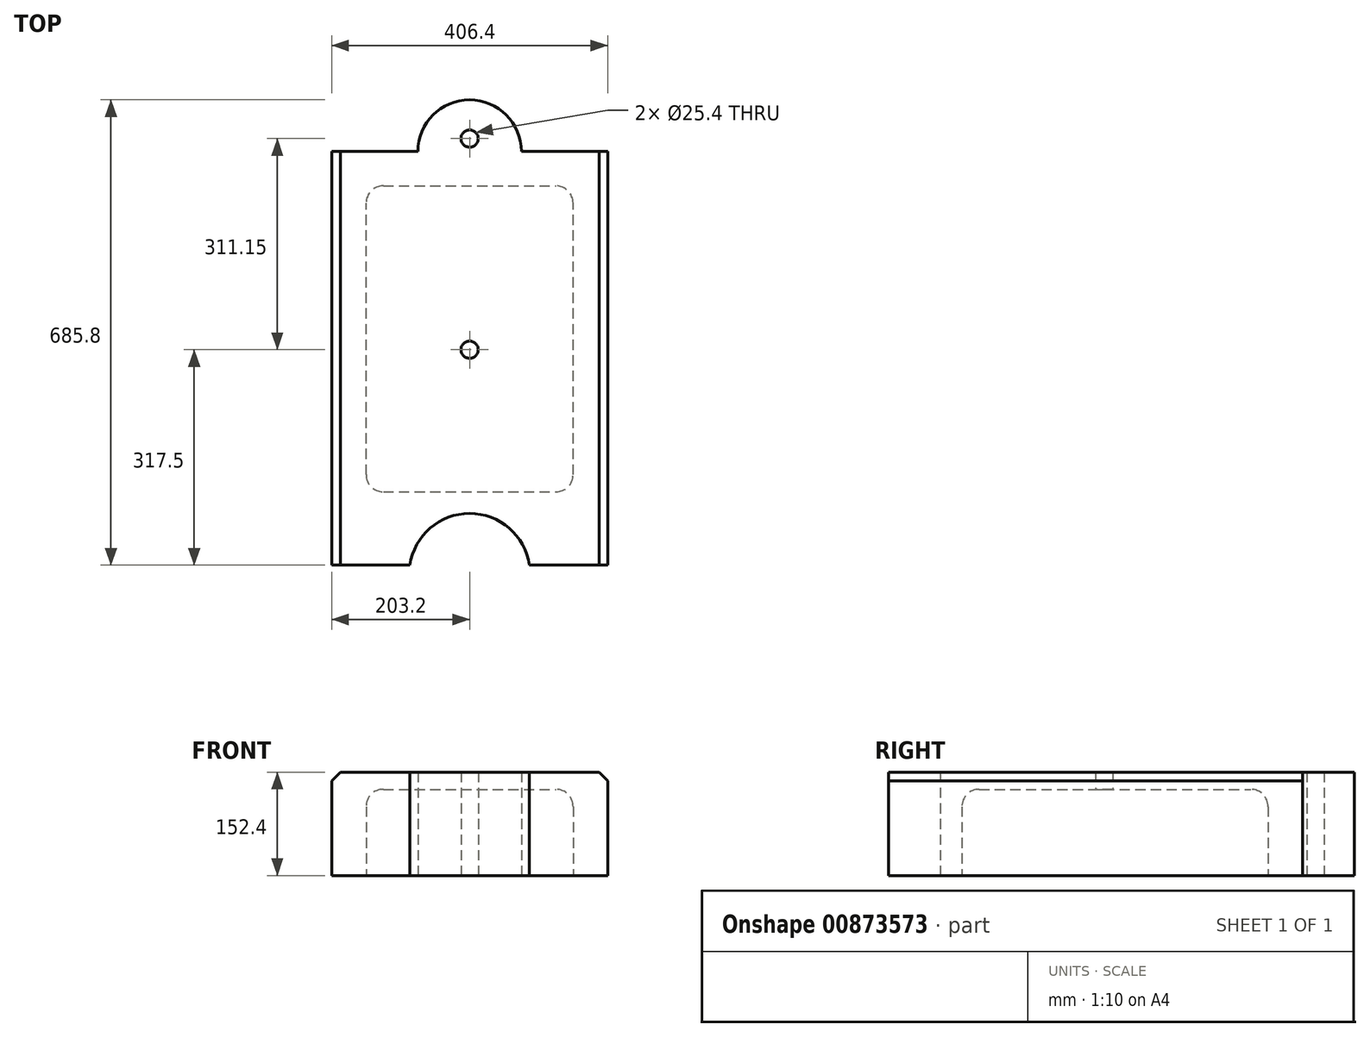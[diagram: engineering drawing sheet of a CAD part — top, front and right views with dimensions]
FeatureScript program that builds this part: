
annotation { "Feature Type Name" : "Feature", "Feature Type Description" : "" }
export const myFeature = defineFeature(function(context is Context, id is Id, definition is map)
    precondition{}
    {
        {
            var Q0;
            Q0=qCreatedBy(makeId("Top.planeOp"),FACE);
            var sketch = newSketch(context, id + "F0", { "sketchPlane" : qUnion([Q0])});
            skLineSegment(sketch, "E0.top", {"start": v(0, 609.6) * mm, "end": v(127, 609.6) * mm});
            skLineSegment(sketch, "E0.left", {"start": v(0, 0) * mm, "end": v(0, 609.6) * mm});
            skLineSegment(sketch, "E0.right", {"start": v(406.4, 0) * mm, "end": v(406.4, 609.6) * mm});
            skLineSegment(sketch, "E1", {"start": v(203.2, 609.6) * mm, "end": v(203.2, -240.43) * mm, "construction": true});
            skArc(sketch, "E2", {"start": v(279.4, 609.6) * mm, "mid": v(203.2, 685.8) * mm, "end": v(127, 609.6) * mm});
            skLineSegment(sketch, "E3.trimOffspring", {"start": v(279.4, 609.6) * mm, "end": v(406.4, 609.6) * mm});
            skLineSegment(sketch, "E4", {"start": v(0, 0) * mm, "end": v(115.21, 0) * mm});
            skLineSegment(sketch, "E5.0", {"start": v(0, -12.7) * mm, "end": v(406.4, -12.7) * mm, "construction": true});
            skArc(sketch, "E6", {"start": v(291.19, 0) * mm, "mid": v(203.2, 76.2) * mm, "end": v(115.21, 0) * mm});
            skLineSegment(sketch, "E7.trimOffspring", {"start": v(291.19, 0) * mm, "end": v(406.4, 0) * mm});
            skLineSegment(sketch, "E8", {"start": v(0, 609.6) * mm, "end": v(520.8, 609.6) * mm, "construction": true});
            skPoint(sketch, "E8.endSnap0", {"position": v(63.5, 609.6) * mm});
            skLineSegment(sketch, "E9.0", {"start": v(0, 628.65) * mm, "end": v(520.8, 628.65) * mm, "construction": true});
            skCircle(sketch, "E10", {"center": v(203.2, 628.65) * mm, "radius": 12.7 * mm});
            skCircle(sketch, "E11", {"center": v(203.2, 317.5) * mm, "radius": 12.7 * mm});
            skLineSegment(sketch, "E12.direction1", {"start": v(203.2, 628.65) * mm, "end": v(228.6, 628.65) * mm, "construction": true});
            skLineSegment(sketch, "E12.direction2", {"start": v(203.2, 628.65) * mm, "end": v(203.2, 311.15) * mm, "construction": true});
            skSolve(sketch);
        }
        {
            var Q0;
            Q0 = qSketchRegion(id + "F0", true);
            extrude(context, id + "F1", {"entities" : qUnion([Q0]), "depth" : 152.4 * mm, "offsetDistance" : 25.4 * mm});
        }
        {
            var Q0;
            Q0=makeQuery(id+"F1.opExtrude","CAP_FACE",FACE,{"disambiguationData":[OSD([sQuery(id+"F0.wireOp",EDGE,"E0.top"),sQuery(id+"F0.wireOp",EDGE,"E0.left"),sQuery(id+"F0.wireOp",EDGE,"E0.right"),sQuery(id+"F0.wireOp",EDGE,"E2"),sQuery(id+"F0.wireOp",EDGE,"E3.trimOffspring"),sQuery(id+"F0.wireOp",EDGE,"E4"),sQuery(id+"F0.wireOp",EDGE,"E6"),sQuery(id+"F0.wireOp",EDGE,"E7.trimOffspring"),sQuery(id+"F0.wireOp",EDGE,"E10"),sQuery(id+"F0.wireOp",EDGE,"E11")])],"isStart":true});
            var sketch = newSketch(context, id + "F2", { "sketchPlane" : qUnion([Q0])});
            skLineSegment(sketch, "E13.1", {"start": v(50.8, -133.35) * mm, "end": v(50.8, -533.4) * mm});
            skLineSegment(sketch, "E13.4", {"start": v(355.6, -133.35) * mm, "end": v(355.6, -533.4) * mm});
            skLineSegment(sketch, "E14", {"start": v(76.2, -107.95) * mm, "end": v(330.2, -107.95) * mm});
            skPoint(sketch, "E14.startSnap0", {"position": v(203.2, -107.95) * mm});
            skLineSegment(sketch, "E15", {"start": v(76.2, -558.8) * mm, "end": v(330.2, -558.8) * mm});
            skPoint(sketch, "E16.visualSharp", {"position": v(50.8, -107.95) * mm});
            skArc(sketch, "E16.filletArc", {"start": v(76.2, -107.95) * mm, "mid": v(58.24, -115.39) * mm, "end": v(50.8, -133.35) * mm});
            skPoint(sketch, "E17.visualSharp", {"position": v(355.6, -107.95) * mm});
            skArc(sketch, "E17.filletArc", {"start": v(355.6, -133.35) * mm, "mid": v(348.16, -115.39) * mm, "end": v(330.2, -107.95) * mm});
            skPoint(sketch, "E18.visualSharp", {"position": v(355.6, -558.8) * mm});
            skArc(sketch, "E18.filletArc", {"start": v(330.2, -558.8) * mm, "mid": v(348.16, -551.36) * mm, "end": v(355.6, -533.4) * mm});
            skPoint(sketch, "E19.visualSharp", {"position": v(50.8, -558.8) * mm});
            skArc(sketch, "E19.filletArc", {"start": v(50.8, -533.4) * mm, "mid": v(58.24, -551.36) * mm, "end": v(76.2, -558.8) * mm});
            skSolve(sketch);
        }
        {
            var Q0;
            Q0 = qSketchRegion(id + "F2", true);
            extrude(context, id + "F3", {"entities" : qUnion([Q0]), "operationType" : NewBodyOperationType.REMOVE, "oppositeDirection" : true, "depth" : 127 * mm, "offsetDistance" : 25.4 * mm});
        }
        {
            var Q0;
            Q0=makeQuery(id+"F3.boolean.opBoolean","COPY",EDGE,{"derivedFrom":makeQuery(id+"F3.opExtrude","CAP_EDGE",EDGE,{"disambiguationData":[OSD([sQuery(id+"F2.wireOp",EDGE,"E13.1")])],"isStart":false})});
            fillet(context, id + "F4", {"entities" : qUnion([Q0]), "radius" : 25.4 * mm, "tangentPropagation" : true, "allowEdgeOverflow" : false});
        }
        {
            var Q0;
            Q0=makeQuery(id+"F1.opExtrude","CAP_EDGE",EDGE,{"disambiguationData":[OSD([sQuery(id+"F0.wireOp",EDGE,"E0.right")])],"isStart":false});
            var Q1;
            Q1=makeQuery(id+"F1.opExtrude","CAP_EDGE",EDGE,{"disambiguationData":[OSD([sQuery(id+"F0.wireOp",EDGE,"E0.left")])],"isStart":false});
            chamfer(context, id + "F5", {"entities" : qUnion([Q0, Q1]), "width" : 12.7 * mm, "tangentPropagation" : true});
        }
    });
